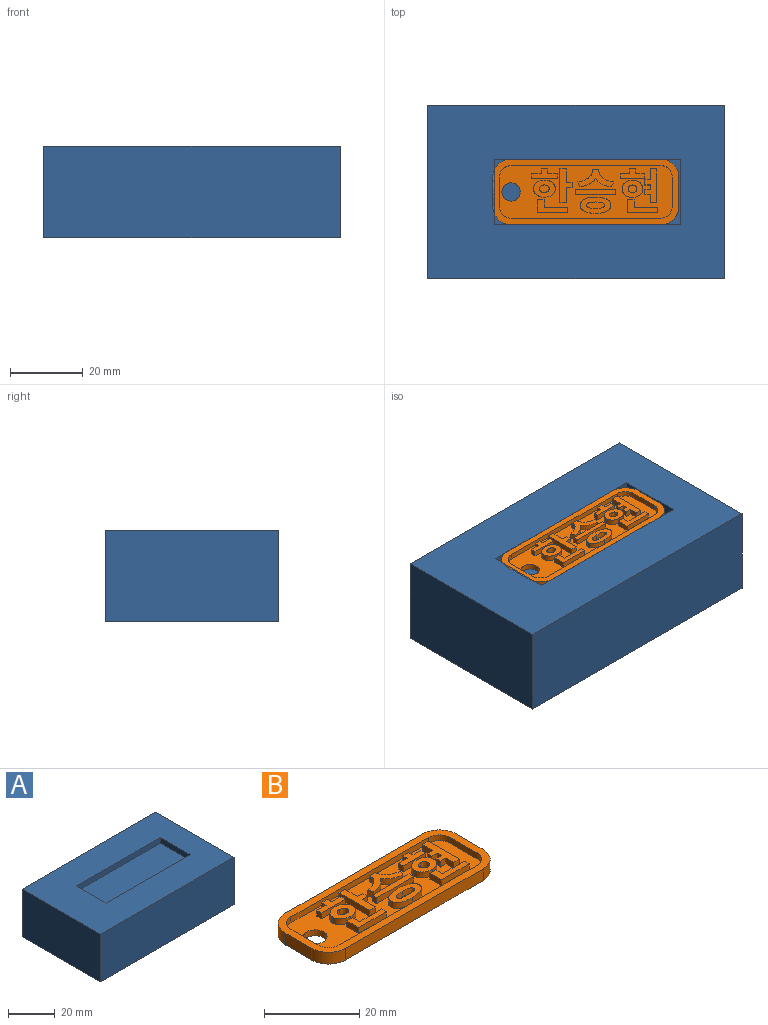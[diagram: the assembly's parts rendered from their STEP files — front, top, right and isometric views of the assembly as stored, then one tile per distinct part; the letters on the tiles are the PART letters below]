
ASSEMBLY  parts=2 mates=1
PART A: 11 faces, bbox 81.1x47.6x25 mm
  f0: plane 81.15x47.55mm, normal (0,0,1), area 2940.7mm2, adj f1,f2,f3,f4,f6,f7,f8,f9
  f1: plane 47.55x25mm, normal (-1,0,0), area 1188.8mm2, adj f0,f2,f4,f5
  f2: plane 81.15x25mm, normal (0,-1,0), area 2028.7mm2, adj f0,f1,f3,f5
  f3: plane 47.55x25mm, normal (1,0,0), area 1188.8mm2, adj f0,f2,f4,f5
  f4: plane 81.15x25mm, normal (0,1,0), area 2028.7mm2, adj f0,f1,f3,f5
  f5: plane 81.15x47.55mm, normal (0,0,-1), area 3858.7mm2, adj f1,f2,f3,f4
  f6: plane 18x3mm, normal (1,0,0), area 54mm2, adj f0,f7,f9,f10
  f7: plane 51x3mm, normal (0,1,0), area 153mm2, adj f0,f6,f8,f10
  f8: plane 18x3mm, normal (-1,0,0), area 54mm2, adj f0,f7,f9,f10
  f9: plane 51x3mm, normal (0,-1,0), area 153mm2, adj f0,f6,f8,f10
  f10: plane 51x18mm, normal (0,0,1), area 918mm2, adj f6,f7,f8,f9
PART B: 119 faces, bbox 51x18x3 mm
  f0: plane 47.4x14.4mm, normal (0,0,1), area 454.4mm2, adj f5,f11,f12,f13,f14,f15,f16,f17
  f1: plane 8x3mm, normal (-1,0,0), area 24mm2, adj f6,f7,f10,f19
  f2: plane 41x3mm, normal (0,-1,0), area 123mm2, adj f6,f7,f8,f19
  f3: plane 8x3mm, normal (1,0,0), area 24mm2, adj f6,f8,f9,f19
  f4: plane 41x3mm, normal (0,1,0), area 123mm2, adj f6,f9,f10,f19
  f5: cylinder r=2.5mm len=5mm, axis (0,0,-1), area 23.6mm2, adj f0,f6
  f6: plane 51x18mm, normal (0,0,-1), area 876.9mm2, adj f1,f2,f3,f4,f5,f7,f8,f9
  f7: cylinder r=5mm len=5mm, axis (0,0,1), area 23.6mm2, adj f1,f2,f6,f19
  f8: cylinder r=5mm len=5mm, axis (0,0,-1), area 23.6mm2, adj f2,f3,f6,f19
  f9: cylinder r=5mm len=5mm, axis (0,0,1), area 23.6mm2, adj f3,f4,f6,f19
  f10: cylinder r=5mm len=5mm, axis (0,0,-1), area 23.6mm2, adj f1,f4,f6,f19
  f11: cylinder r=3.2mm len=3.2mm, axis (0,0,-1), area 7.5mm2, adj f0,f12,f18,f19
  f12: plane 8x1.5mm, normal (1,0,0), area 12mm2, adj f0,f11,f13,f19
  f13: cylinder r=3.2mm len=3.2mm, axis (0,0,-1), area 7.5mm2, adj f0,f12,f14,f19
  f14: plane 41x1.5mm, normal (0,-1,0), area 61.5mm2, adj f0,f13,f15,f19
  f15: cylinder r=3.2mm len=3.2mm, axis (0,0,-1), area 7.5mm2, adj f0,f14,f16,f19
  f16: plane 8x1.5mm, normal (-1,0,0), area 12mm2, adj f0,f15,f17,f19
  f17: cylinder r=3.2mm len=3.2mm, axis (0,0,-1), area 7.5mm2, adj f0,f16,f18,f19
  f18: plane 41x1.5mm, normal (0,1,0), area 61.5mm2, adj f0,f11,f17,f19
  f19: plane 51x18mm, normal (0,0,1), area 222.8mm2, adj f1,f2,f3,f4,f7,f8,f9,f10
  f20: plane 1.5x1.36mm, normal (1,-0.01,0), area 2mm2, adj f0,f21,f27,f28
  f21: plane 2.72x1.5mm, normal (0,1,0), area 4.1mm2, adj f0,f20,f22,f28
  f22: plane 1.5x1.29mm, normal (1,0,0), area 1.9mm2, adj f0,f21,f23,f28
  f23: plane 1.75x1.5mm, normal (0,1,0), area 2.6mm2, adj f0,f22,f24,f28
  f24: plane 1.5x1.29mm, normal (-1,0,0), area 1.9mm2, adj f0,f23,f25,f28
  f25: plane 2.69x1.5mm, normal (0,1,0), area 4mm2, adj f0,f24,f26,f28
  f26: plane 1.5x1.36mm, normal (-1,0,0), area 2mm2, adj f0,f25,f27,f28
  f27: plane 7.15x1.5mm, normal (0,-1,0), area 10.7mm2, adj f0,f20,f26,f28
  f28: plane 7.16x2.65mm, normal (0,0,1), area 12mm2, adj f20,f21,f22,f23,f24,f25,f26,f27
  f29: extruded ~1.5x1.32mm, area 2.8mm2, adj f30,f36,f37,f38
  f30: extruded ~1.5x1.32mm, area 2.8mm2, adj f29,f31,f37,f38
  f31: extruded ~1.5x1.32mm, area 2.8mm2, adj f30,f36,f37,f38
  f32: extruded ~2.98x2.35mm, area 6.4mm2, adj f0,f33,f35,f37
  f33: extruded ~2.98x2.33mm, area 6.3mm2, adj f0,f32,f34,f37
  f34: extruded ~2.98x2.33mm, area 6.3mm2, adj f0,f33,f35,f37
  f35: extruded ~2.98x2.35mm, area 6.4mm2, adj f0,f32,f34,f37
  f36: extruded ~1.5x1.32mm, area 2.8mm2, adj f29,f31,f37,f38
  f37: plane 5.96x4.68mm, normal (0,0,1), area 18mm2, adj f29,f30,f31,f32,f33,f34,f35,f36
  f38: plane 2.64x2.04mm, normal (0,0,1), area 4.4mm2, adj f29,f30,f31,f36
  f39: plane 2.14x1.5mm, normal (1,0,0), area 3.2mm2, adj f0,f40,f44,f45
  f40: plane 1.74x1.5mm, normal (0,1,0), area 2.6mm2, adj f0,f39,f41,f45
  f41: plane 3.52x1.5mm, normal (-1,0,0), area 5.3mm2, adj f0,f40,f42,f45
  f42: plane 8.27x1.5mm, normal (0,-1,0), area 12.4mm2, adj f0,f41,f43,f45
  f43: plane 1.5x1.38mm, normal (1,0,0), area 2.1mm2, adj f0,f42,f44,f45
  f44: plane 6.53x1.5mm, normal (0,1,0), area 9.8mm2, adj f0,f39,f43,f45
  f45: plane 8.27x3.52mm, normal (0,0,1), area 15.2mm2, adj f39,f40,f41,f42,f43,f44
  f46: plane 1.61x1.5mm, normal (0,1,0), area 2.4mm2, adj f0,f47,f53,f54
  f47: plane 3.71x1.5mm, normal (1,0,0), area 5.6mm2, adj f0,f46,f48,f54
  f48: plane 1.74x1.5mm, normal (0,1,0), area 2.6mm2, adj f0,f47,f49,f54
  f49: plane 9.09x1.5mm, normal (-1,0,0), area 13.6mm2, adj f0,f48,f50,f54
  f50: plane 1.74x1.5mm, normal (0,-1,0), area 2.6mm2, adj f0,f49,f51,f54
  f51: plane 3.94x1.5mm, normal (1,0,0), area 5.9mm2, adj f0,f50,f52,f54
  f52: plane 1.61x1.5mm, normal (0,-1,0), area 2.4mm2, adj f0,f51,f53,f54
  f53: plane 1.5x1.44mm, normal (1,0,0), area 2.2mm2, adj f0,f46,f52,f54
  f54: plane 9.09x3.35mm, normal (0,0,1), area 18.1mm2, adj f46,f47,f48,f49,f50,f51,f52,f53
  f55: plane 1.5x1.36mm, normal (0.91,-0.41,0), area 2.2mm2, adj f0,f56,f63,f64
  f56: extruded ~4.05x3.01mm, area 8.2mm2, adj f0,f55,f57,f64
  f57: plane 1.5x0.36mm, normal (1,0,0), area 0.5mm2, adj f0,f56,f58,f64
  f58: plane 1.79x1.5mm, normal (0,1,0), area 2.7mm2, adj f0,f57,f59,f64
  f59: plane 1.5x0.36mm, normal (-1,0,0), area 0.5mm2, adj f0,f58,f60,f64
  f60: extruded ~4.05x3.01mm, area 8.2mm2, adj f0,f59,f61,f64
  f61: plane 1.5x1.36mm, normal (-0.91,-0.42,0), area 2.2mm2, adj f0,f60,f62,f64
  f62: extruded ~4.31x2.35mm, area 7.6mm2, adj f0,f61,f63,f64
  f63: extruded ~4.33x2.35mm, area 7.6mm2, adj f0,f55,f62,f64
  f64: plane 9.89x4.72mm, normal (0,0,1), area 18mm2, adj f55,f56,f57,f58,f59,f60,f61,f62
  f65: extruded ~2.45x1.5mm, area 4.3mm2, adj f66,f72,f73,f74
  f66: extruded ~2.45x1.5mm, area 4.3mm2, adj f65,f67,f73,f74
  f67: extruded ~2.45x1.5mm, area 4.3mm2, adj f66,f72,f73,f74
  f68: extruded ~4.22x2.2mm, area 7.9mm2, adj f0,f69,f71,f73
  f69: extruded ~4.21x2.2mm, area 7.9mm2, adj f0,f68,f70,f73
  f70: extruded ~4.21x2.22mm, area 7.9mm2, adj f0,f69,f71,f73
  f71: extruded ~4.22x2.22mm, area 7.9mm2, adj f0,f68,f70,f73
  f72: extruded ~2.45x1.5mm, area 4.3mm2, adj f65,f67,f73,f74
  f73: plane 8.43x4.42mm, normal (0,0,1), area 23.1mm2, adj f65,f66,f67,f68,f69,f70,f71,f72
  f74: plane 4.91x1.79mm, normal (0,0,1), area 7.4mm2, adj f65,f66,f67,f72
  f75: plane 10.97x1.5mm, normal (0,1,0), area 16.5mm2, adj f0,f76,f78,f79
  f76: plane 1.5x1.37mm, normal (-1,0,0), area 2.1mm2, adj f0,f75,f77,f79
  f77: plane 10.97x1.5mm, normal (0,-1,0), area 16.5mm2, adj f0,f76,f78,f79
  f78: plane 1.5x1.37mm, normal (1,0,0), area 2.1mm2, adj f0,f75,f77,f79
  f79: plane 10.97x1.37mm, normal (0,0,1), area 15.1mm2, adj f75,f76,f77,f78
  f80: plane 2.26x1.5mm, normal (-1,0,0), area 3.4mm2, adj f0,f81,f91,f92
  f81: plane 1.74x1.5mm, normal (0,-1,0), area 2.6mm2, adj f0,f80,f82,f92
  f82: plane 9.26x1.5mm, normal (1,0,0), area 13.9mm2, adj f0,f81,f83,f92
  f83: plane 1.74x1.5mm, normal (0,1,0), area 2.6mm2, adj f0,f82,f84,f92
  f84: plane 3.02x1.5mm, normal (-1,0,0), area 4.5mm2, adj f0,f83,f85,f92
  f85: plane 1.58x1.5mm, normal (0,1,0), area 2.4mm2, adj f0,f84,f86,f92
  f86: plane 1.5x1.38mm, normal (-1,0,0), area 2.1mm2, adj f0,f85,f87,f92
  f87: plane 1.58x1.5mm, normal (0,-1,0), area 2.4mm2, adj f0,f86,f88,f92
  f88: plane 1.5x1.21mm, normal (-1,0,0), area 1.8mm2, adj f0,f87,f89,f92
  f89: plane 1.58x1.5mm, normal (0,1,0), area 2.4mm2, adj f0,f88,f90,f92
  f90: plane 1.5x1.38mm, normal (-1,0,0), area 2.1mm2, adj f0,f89,f91,f92
  f91: plane 1.58x1.5mm, normal (0,-1,0), area 2.4mm2, adj f0,f80,f90,f92
  f92: plane 9.26x3.32mm, normal (0,0,1), area 20.5mm2, adj f80,f81,f82,f83,f84,f85,f86,f87
  f93: plane 1.5x1.36mm, normal (1,0,0), area 2mm2, adj f0,f94,f100,f101
  f94: plane 2.37x1.5mm, normal (0,1,0), area 3.6mm2, adj f0,f93,f95,f101
  f95: plane 1.5x1.32mm, normal (1,0,0), area 2mm2, adj f0,f94,f96,f101
  f96: plane 1.74x1.5mm, normal (0,1,0), area 2.6mm2, adj f0,f95,f97,f101
  f97: plane 1.5x1.32mm, normal (-1,0,0), area 2mm2, adj f0,f96,f98,f101
  f98: plane 2.55x1.5mm, normal (0,1,0), area 3.8mm2, adj f0,f97,f99,f101
  f99: plane 1.5x1.36mm, normal (-1,0,0), area 2mm2, adj f0,f98,f100,f101
  f100: plane 6.66x1.5mm, normal (0,-1,0), area 10mm2, adj f0,f93,f99,f101
  f101: plane 6.66x2.68mm, normal (0,0,1), area 11.3mm2, adj f93,f94,f95,f96,f97,f98,f99,f100
  f102: extruded ~1.5x1.21mm, area 2.7mm2, adj f103,f109,f110,f111
  f103: extruded ~1.5x1.21mm, area 2.7mm2, adj f102,f104,f110,f111
  f104: extruded ~1.5x1.2mm, area 2.7mm2, adj f103,f109,f110,f111
  f105: extruded ~2.84x2.4mm, area 6.2mm2, adj f0,f106,f108,f110
  f106: extruded ~2.84x2.37mm, area 6.2mm2, adj f0,f105,f107,f110
  f107: extruded ~2.85x2.37mm, area 6.2mm2, adj f0,f106,f108,f110
  f108: extruded ~2.85x2.4mm, area 6.3mm2, adj f0,f105,f107,f110
  f109: extruded ~1.5x1.2mm, area 2.7mm2, adj f102,f104,f110,f111
  f110: plane 5.68x4.77mm, normal (0,0,1), area 17.6mm2, adj f102,f103,f104,f105,f106,f107,f108,f109
  f111: plane 2.41x2.1mm, normal (0,0,1), area 4.1mm2, adj f102,f103,f104,f109
  f112: plane 6.54x1.5mm, normal (0,1,0), area 9.8mm2, adj f0,f113,f117,f118
  f113: plane 2.04x1.5mm, normal (1,0,0), area 3.1mm2, adj f0,f112,f114,f118
  f114: plane 1.74x1.5mm, normal (0,1,0), area 2.6mm2, adj f0,f113,f115,f118
  f115: plane 3.43x1.5mm, normal (-1,0,0), area 5.1mm2, adj f0,f114,f116,f118
  f116: plane 8.28x1.5mm, normal (0,-1,0), area 12.4mm2, adj f0,f115,f117,f118
  f117: plane 1.5x1.38mm, normal (1,0,0), area 2.1mm2, adj f0,f112,f116,f118
  f118: plane 8.28x3.43mm, normal (0,0,1), area 15mm2, adj f112,f113,f114,f115,f116,f117
PLACE A at identity fixed
PLACE B t=(17.77,14.78,-3)mm
MATE fastened B.f6 <-> A.f10  axis (0,0,-1) through (43.73,23.78,-3)mm
